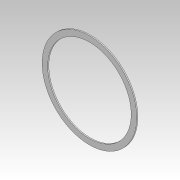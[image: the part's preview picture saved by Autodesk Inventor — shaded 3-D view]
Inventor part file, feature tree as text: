
AUTODESK INVENTOR PART (.ipt)
format: ipt  version: 2020 (Build 240168000, 168)  size: 81,920 bytes
history: native  units: mm
features: extrude x1, sketch x1
ambient origin geometry x8: Origin, YZ Plane, XZ Plane, XY Plane, X Axis, Y Axis, Z Axis, Center Point
bodies: Solid1 (feature_tree)
feature tree (2):
  extrude  "Extrusion1"  Depth=1.0mm
  sketch  "Sketch1"  dims[d0=75.3mm d1=5.0mm d2=1.0mm d3=0.0mm]
